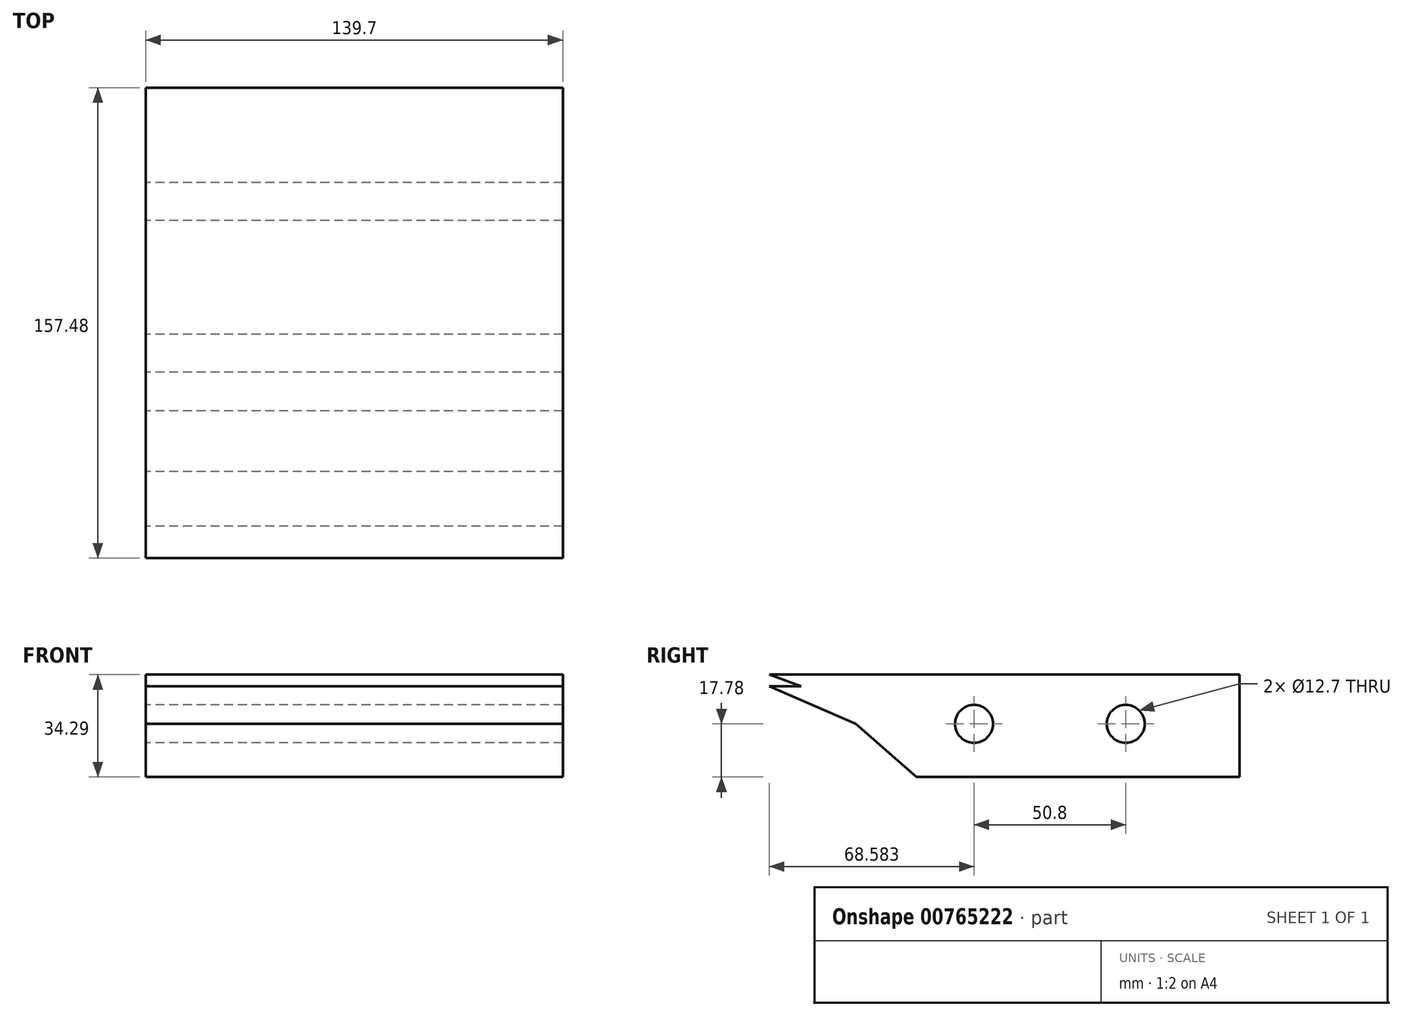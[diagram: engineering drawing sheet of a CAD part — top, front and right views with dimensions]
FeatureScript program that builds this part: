
annotation { "Feature Type Name" : "Feature", "Feature Type Description" : "" }
export const myFeature = defineFeature(function(context is Context, id is Id, definition is map)
    precondition{}
    {
        {
            var Q0;
            Q0=qCreatedBy(makeId("Right.planeOp"),FACE);
            var sketch = newSketch(context, id + "F0", { "sketchPlane" : qUnion([Q0])});
            skLineSegment(sketch, "E0", {"start": v(0, 0) * mm, "end": v(0, 16.51) * mm, "construction": true});
            skLineSegment(sketch, "E1", {"start": v(-46.98, 16.51) * mm, "end": v(-46.98, -17.78) * mm, "construction": true});
            skLineSegment(sketch, "E2", {"start": v(45.67, 16.51) * mm, "end": v(45.67, -17.78) * mm});
            skLineSegment(sketch, "E3", {"start": v(45.67, -17.78) * mm, "end": v(-62.48, -17.78) * mm});
            skLineSegment(sketch, "E4", {"start": v(-62.48, -17.78) * mm, "end": v(-82.82, 0) * mm});
            skLineSegment(sketch, "E5", {"start": v(-82.82, 0) * mm, "end": v(-111.8, 12.6) * mm});
            skLineSegment(sketch, "E6", {"start": v(-111.8, 12.6) * mm, "end": v(-101.07, 12.6) * mm});
            skLineSegment(sketch, "E7", {"start": v(-101.07, 12.6) * mm, "end": v(-111.8, 16.5) * mm});
            skLineSegment(sketch, "E8", {"start": v(45.67, 16.51) * mm, "end": v(-111.8, 16.5) * mm});
            skLineSegment(sketch, "E9", {"start": v(45.67, -17.78) * mm, "end": v(7.57, -17.78) * mm, "construction": true});
            skLineSegment(sketch, "E10", {"start": v(45.67, -24.78) * mm, "end": v(-43.23, -24.78) * mm, "construction": true});
            skCircle(sketch, "E11", {"center": v(7.57, 0) * mm, "radius": 6.35 * mm});
            skCircle(sketch, "E12", {"center": v(-43.23, 0) * mm, "radius": 6.35 * mm});
            skSolve(sketch);
        }
        {
            var Q0;
            Q0 = qSketchRegion(id + "F0", true);
            extrude(context, id + "F1", {"entities" : qUnion([Q0]), "depth" : 139.7 * mm, "offsetDistance" : 25.4 * mm});
        }
    });
